FCSTD DOCUMENT  (FreeCAD 0.22R37100 (Git))
Label: composit_full_size3_model
License: All rights reserved
LicenseURL: http://en.wikipedia.org/wiki/All_rights_reserved
objects: App::Link×22, App::DocumentObjectGroup×4, Part::FeaturePython×4, App::AnnotationLabel×3, PartDesign::CoordinateSystem×1, App::FeaturePython×1, App::Part×1
note: 5 computed .brp shape members not serialized (recipe doc carries the construction recipe); baked Part::Feature solids carry a one-line shape summary decoded from their .brp
EXTERNAL_REF file=composit_full_size3.FCStd obj=Local_CS006
EXTERNAL_REF file=composit_full_size3.FCStd obj=Local_CS024
EXTERNAL_REF file=composit_full_size3.FCStd obj=Body141
EXTERNAL_REF file=composit_full_size3.FCStd obj=Local_CS008
EXTERNAL_REF file=composit_full_size3.FCStd obj=Local_CS009
EXTERNAL_REF file=composit_full_size3.FCStd obj=Body145
EXTERNAL_REF file=composit_full_size3.FCStd obj=Local_CS005
EXTERNAL_REF file=composit_full_size3.FCStd obj=Local_CS007
EXTERNAL_REF file=composit_full_size3.FCStd obj=Body144
EXTERNAL_REF file=composit_full_size3.FCStd obj=Local_CS018
EXTERNAL_REF file=composit_full_size3.FCStd obj=Body008
EXTERNAL_REF file=composit_full_size3.FCStd obj=Local_CS017
EXTERNAL_REF file=composit_full_size3.FCStd obj=Local_CS020
EXTERNAL_REF file=composit_full_size3.FCStd obj=Body006
EXTERNAL_REF file=composit_full_size3.FCStd obj=Local_CS019
EXTERNAL_REF file=composit_full_size3.FCStd obj=Local_CS022
EXTERNAL_REF file=composit_full_size3.FCStd obj=Body105
EXTERNAL_REF file=composit_full_size3.FCStd obj=Local_CS021
EXTERNAL_REF file=hub2108.FCStd obj=Local_CS001
EXTERNAL_REF file=hub2108.FCStd obj=Body
EXTERNAL_REF file=composit_full_size3.FCStd obj=Local_CS013
EXTERNAL_REF file=hub2108.FCStd obj=Local_CS
EXTERNAL_REF file=composit_full_size3.FCStd obj=Body009
EXTERNAL_REF file=composit_full_size3.FCStd obj=Local_CS011
EXTERNAL_REF file=composit_full_size3.FCStd obj=Local_CS012
EXTERNAL_REF file=composit_full_size3.FCStd obj=Body007
EXTERNAL_REF file=composit_full_size3.FCStd obj=Local_CS010
EXTERNAL_REF file=composit_full_size3.FCStd obj=Local_CS015
EXTERNAL_REF file=composit_full_size3.FCStd obj=Body107
EXTERNAL_REF file=composit_full_size3.FCStd obj=Local_CS025
EXTERNAL_REF file=composit_full_size3.FCStd obj=Body
EXTERNAL_REF file=composit_full_size3.FCStd obj=Local_CS027
EXTERNAL_REF file=composit_full_size3.FCStd obj=Body001
EXTERNAL_REF file=composit_full_size3.FCStd obj=Local_CS026
EXTERNAL_REF file=composit_full_size3.FCStd obj=Local_CS029
EXTERNAL_REF file=composit_full_size3.FCStd obj=Body004
EXTERNAL_REF file=composit_full_size3.FCStd obj=Local_CS030
EXTERNAL_REF file=composit_full_size3.FCStd obj=Local_CS032
EXTERNAL_REF file=composit_full_size3.FCStd obj=Body110
EXTERNAL_REF file=composit_full_size3.FCStd obj=Local_CS038
EXTERNAL_REF file=composit_full_size3.FCStd obj=Local_CS040
EXTERNAL_REF file=composit_full_size3.FCStd obj=Body142
EXTERNAL_REF file=composit_full_size3.FCStd obj=Local_CS031
EXTERNAL_REF file=composit_full_size3.FCStd obj=Local_CS039
EXTERNAL_REF file=composit_full_size3.FCStd obj=Body123
EXTERNAL_REF file=composit_full_size3.FCStd obj=Local_CS023
EXTERNAL_REF file=composit_full_size3.FCStd obj=Local_CS043
EXTERNAL_REF file=composit_full_size3.FCStd obj=Body147
EXTERNAL_REF file=composit_full_size3.FCStd obj=Local_CS044
EXTERNAL_REF file=composit_full_size3.FCStd obj=Body143
EXTERNAL_REF file=composit_full_size3.FCStd obj=Local_CS047
EXTERNAL_REF file=composit_full_size3.FCStd obj=pillar_bottom_LCS
EXTERNAL_REF file=composit_full_size3.FCStd obj=Body011
EXTERNAL_REF file=composit_full_size3.FCStd obj=Local_CS049
EXTERNAL_REF file=composit_full_size3.FCStd obj=Body152
EXTERNAL_REF file=composit_full_size3.FCStd obj=Local_CS050
EXTERNAL_REF file=composit_full_size3.FCStd obj=Body146

FEATURE [App::DocumentObjectGroup] Parts
FEATURE [PartDesign::CoordinateSystem] LCS_Origin
  AttacherType = Attacher::AttachEngine3D
  AttachmentSupport = -> [X_Axis]
  MapMode = 2
FEATURE [App::DocumentObjectGroup] Constraints
FEATURE [App::FeaturePython] Variables  # WARN: FeaturePython — macro-defined, semantics opaque (R4)
  Type = App::PropertyContainer
FEATURE [App::DocumentObjectGroup] Configurations
FEATURE [App::Link] pillar3
  AttachedBy = #Local_CS006
  AttachedTo = basement_bottom_proxy#Local_CS024
  LinkPlacement = pos=(332.554,-192,-90) rot=(0,0,1;1.0472rad)
  LinkedObject = -> <external composit_full_size3.FCStd>#Body141
  Placement = pos=(332.554,-192,-90) rot=(0,0,1;1.0472rad)
  SolverId = Asm4EE
  expr: Placement = basement_bottom_proxy.Placement * composit_full_size3#Local_CS024.Placement * AttachmentOffset * composit_full_size3#Local_CS006.Placement ^ -1
FEATURE [App::Link] pilllar3_dec_corner
  AttachedBy = #Local_CS008
  AttachedTo = pillar3#Local_CS009
  LinkPlacement = pos=(332.554,-192,380) rot=(0,0,1;1.0472rad)
  LinkedObject = -> <external composit_full_size3.FCStd>#Body145
  Placement = pos=(332.554,-192,380) rot=(0,0,1;1.0472rad)
  SolverId = Asm4EE
  expr: Placement = pillar3.Placement * composit_full_size3#Local_CS009.Placement * AttachmentOffset * composit_full_size3#Local_CS008.Placement ^ -1
FEATURE [App::Link] pillar3_hat_fix
  AttachedBy = #Local_CS005
  AttachedTo = pillar3#Local_CS007
  LinkPlacement = pos=(330.822,-191,1504) rot=(0,0,1;1.0472rad)
  LinkedObject = -> <external composit_full_size3.FCStd>#Body144
  Placement = pos=(330.822,-191,1504) rot=(0,0,1;1.0472rad)
  SolverId = Asm4EE
  expr: Placement = pillar3.Placement * composit_full_size3#Local_CS007.Placement * AttachmentOffset * composit_full_size3#Local_CS005.Placement ^ -1
FEATURE [App::Link] basement_top_proxy
  AttachedBy = #Local_CS018
  AttachedTo = Parent Assembly#LCS_Origin
  LinkPlacement = pos=(0,0,-3) rot=(0,0,1;0rad)
  LinkedObject = -> <external composit_full_size3.FCStd>#Body008
  Placement = pos=(0,0,-3) rot=(0,0,1;0rad)
  SolverId = Asm4EE
  expr: Placement = LCS_Origin.Placement * AttachmentOffset * composit_full_size3#Local_CS018.Placement ^ -1
FEATURE [App::Link] basement_top_plywood
  AttachedBy = #Local_CS020
  AttachedTo = basement_top_proxy#Local_CS017
  LinkPlacement = pos=(0,0,-21) rot=(0,0,1;0rad)
  LinkedObject = -> <external composit_full_size3.FCStd>#Body006
  Placement = pos=(0,0,-21) rot=(0,0,1;0rad)
  SolverId = Asm4EE
  expr: Placement = basement_top_proxy.Placement * composit_full_size3#Local_CS017.Placement * AttachmentOffset * composit_full_size3#Local_CS020.Placement ^ -1
FEATURE [App::Link] basement_top_amplifier_material_0_50ansi  label="basement_top_amplifier_material_0.50ansi"
  AttachedBy = #Local_CS022
  AttachedTo = basement_top_plywood#Local_CS019
  LinkPlacement = pos=(0,0,-23) rot=(0,0,1;0rad)
  LinkedObject = -> <external composit_full_size3.FCStd>#Body105
  Placement = pos=(0,0,-23) rot=(0,0,1;0rad)
  SolverId = Asm4EE
  expr: Placement = basement_top_plywood.Placement * composit_full_size3#Local_CS019.Placement * AttachmentOffset * composit_full_size3#Local_CS022.Placement ^ -1
FEATURE [App::Link] hub2108
  AttachedBy = #Local_CS001
  AttachedTo = basement_top_amplifier_material_0_50ansi#Local_CS021
  LinkPlacement = pos=(0,0,-90) rot=(0,0,1;0rad)
  LinkedObject = -> <external hub2108.FCStd>#Body
  Placement = pos=(0,0,-90) rot=(0,0,1;0rad)
  SolverId = Asm4EE
  expr: Placement = basement_top_amplifier_material_0_50ansi.Placement * composit_full_size3#Local_CS021.Placement * AttachmentOffset * hub2108#Local_CS001.Placement ^ -1
FEATURE [App::Link] basement_bottom_proxy
  AttachedBy = #Local_CS013
  AttachedTo = hub2108#Local_CS
  LinkPlacement = pos=(0,0,-93) rot=(0,0,1;0rad)
  LinkedObject = -> <external composit_full_size3.FCStd>#Body009
  Placement = pos=(0,0,-93) rot=(0,0,1;0rad)
  SolverId = Asm4EE
  expr: Placement = hub2108.Placement * hub2108#Local_CS.Placement * AttachmentOffset * composit_full_size3#Local_CS013.Placement ^ -1
FEATURE [App::Link] basement_bottom_plywood
  AttachedBy = #Local_CS011
  AttachedTo = basement_bottom_proxy#Local_CS012
  LinkPlacement = pos=(0,0,-111) rot=(0,0,1;0rad)
  LinkedObject = -> <external composit_full_size3.FCStd>#Body007
  Placement = pos=(0,0,-111) rot=(0,0,1;0rad)
  SolverId = Asm4EE
  expr: Placement = basement_bottom_proxy.Placement * composit_full_size3#Local_CS012.Placement * AttachmentOffset * composit_full_size3#Local_CS011.Placement ^ -1
FEATURE [App::Link] basement_bottom_amplifier_material_0_50ansi  label="basement_bottom_amplifier_material_0.50ansi"
  AttachedBy = #Local_CS015
  AttachedTo = basement_bottom_plywood#Local_CS010
  LinkPlacement = pos=(0,0,-113) rot=(0,0,1;0rad)
  LinkedObject = -> <external composit_full_size3.FCStd>#Body107
  Placement = pos=(0,0,-113) rot=(0,0,1;0rad)
  SolverId = Asm4EE
  expr: Placement = basement_bottom_plywood.Placement * composit_full_size3#Local_CS010.Placement * AttachmentOffset * composit_full_size3#Local_CS015.Placement ^ -1
FEATURE [App::Link] part1_material_0_30ansi  label="part1_material_0.30ansi"
  AttachedBy = #Local_CS025
  AttachedTo = basement_top_proxy#Local_CS018
  AttachmentOffset = pos=(0,0,0) rot=(0,0,1;4.18879rad)
  LinkPlacement = pos=(0,0,0) rot=(0,0,1;4.18879rad)
  LinkedObject = -> <external composit_full_size3.FCStd>#Body
  Placement = pos=(0,0,0) rot=(0,0,1;4.18879rad)
  SolverId = Asm4EE
  expr: Placement = basement_top_proxy.Placement * composit_full_size3#Local_CS018.Placement * AttachmentOffset * composit_full_size3#Local_CS025.Placement ^ -1
FEATURE [App::Link] part2_material_0_30ansi  label="part2_material_0.30ansi"
  AttachedBy = #Local_CS027
  AttachedTo = part1_material_0_30ansi#Local_CS025
  AttachmentOffset = pos=(0,0,0) rot=(0,0,1;2.0944rad)
  LinkPlacement = pos=(0,0,0) rot=(0,0,1;4.18879rad)
  LinkedObject = -> <external composit_full_size3.FCStd>#Body001
  Placement = pos=(0,0,0) rot=(0,0,1;4.18879rad)
  SolverId = Asm4EE
  expr: Placement = part1_material_0_30ansi.Placement * composit_full_size3#Local_CS025.Placement * AttachmentOffset * composit_full_size3#Local_CS027.Placement ^ -1
FEATURE [App::Link] dropper_fix_bottom
  AttachedBy = #Local_CS029
  AttachedTo = part1_material_0_30ansi#Local_CS026
  LinkPlacement = pos=(0,0,1428) rot=(0,0,1;4.18879rad)
  LinkedObject = -> <external composit_full_size3.FCStd>#Body004
  Placement = pos=(0,0,1428) rot=(0,0,1;4.18879rad)
  SolverId = Asm4EE
  expr: Placement = part1_material_0_30ansi.Placement * composit_full_size3#Local_CS026.Placement * AttachmentOffset * composit_full_size3#Local_CS029.Placement ^ -1
FEATURE [App::Link] dropper_fix_top
  AttachedBy = #Local_CS032
  AttachedTo = dropper_fix_bottom#Local_CS030
  AttachmentOffset = pos=(0,0,0) rot=(0,1,0;3.14159rad)
  LinkPlacement = pos=(2e-16,3e-16,1434) rot=(-0.866025,-0.5,0;3.14159rad)
  LinkedObject = -> <external composit_full_size3.FCStd>#Body110
  Placement = pos=(2e-16,3e-16,1434) rot=(-0.866025,-0.5,0;3.14159rad)
  SolverId = Asm4EE
  expr: Placement = dropper_fix_bottom.Placement * composit_full_size3#Local_CS030.Placement * AttachmentOffset * composit_full_size3#Local_CS032.Placement ^ -1
FEATURE [App::Link] hat3_bottom
  AttachedBy = #Local_CS038
  AttachedTo = sleeve_outer#Local_CS040
  AttachmentOffset = pos=(0,0,3) rot=(0,0,1;0rad)
  LinkPlacement = pos=(-1.14e-14,7e-15,1501) rot=(0,0,1;4.18879rad)
  LinkedObject = -> <external composit_full_size3.FCStd>#Body142
  Placement = pos=(-1.14e-14,7e-15,1501) rot=(0,0,1;4.18879rad)
  SolverId = Asm4EE
  expr: Placement = sleeve_outer.Placement * composit_full_size3#Local_CS040.Placement * AttachmentOffset * composit_full_size3#Local_CS038.Placement ^ -1
FEATURE [App::Link] sleeve_outer
  AttachedBy = #Local_CS039
  AttachedTo = dropper_fix_top#Local_CS031
  AttachmentOffset = pos=(0,0,0) rot=(0,-1,0;3.14159rad)
  LinkPlacement = pos=(2e-16,3e-16,1434) rot=(0,0,1;4.18879rad)
  LinkedObject = -> <external composit_full_size3.FCStd>#Body123
  Placement = pos=(2e-16,3e-16,1434) rot=(0,0,1;4.18879rad)
  SolverId = Asm4EE
  expr: Placement = dropper_fix_top.Placement * composit_full_size3#Local_CS031.Placement * AttachmentOffset * composit_full_size3#Local_CS039.Placement ^ -1
FEATURE [App::Link] pillar004
  AttachedBy = #Local_CS006
  AttachedTo = basement_bottom_proxy#Local_CS023
  LinkPlacement = pos=(-332.554,-192,-90) rot=(0,0,-1;1.0472rad)
  LinkedObject = -> <external composit_full_size3.FCStd>#Body141
  Placement = pos=(-332.554,-192,-90) rot=(0,0,-1;1.0472rad)
  SolverId = Asm4EE
  expr: Placement = basement_bottom_proxy.Placement * composit_full_size3#Local_CS023.Placement * AttachmentOffset * composit_full_size3#Local_CS006.Placement ^ -1
FEATURE [App::Link] pilllar3_dec_corner_mirror
  AttachedBy = #Local_CS043
  AttachedTo = pillar004#Local_CS009
  LinkPlacement = pos=(-332.554,-192,380) rot=(0,0,-1;1.0472rad)
  LinkedObject = -> <external composit_full_size3.FCStd>#Body147
  Placement = pos=(-332.554,-192,380) rot=(0,0,-1;1.0472rad)
  SolverId = Asm4EE
  expr: Placement = pillar004.Placement * composit_full_size3#Local_CS009.Placement * AttachmentOffset * composit_full_size3#Local_CS043.Placement ^ -1
FEATURE [App::Link] hat3_cap
  AttachedBy = #Local_CS044
  AttachedTo = sleeve_outer#Local_CS040
  AttachmentOffset = pos=(0,0,87) rot=(0,0,1;0rad)
  LinkPlacement = pos=(-2.65e-14,1.57e-14,1588) rot=(0,0,1;4.18879rad)
  LinkedObject = -> <external composit_full_size3.FCStd>#Body143
  Placement = pos=(-2.65e-14,1.57e-14,1588) rot=(0,0,1;4.18879rad)
  SolverId = Asm4EE
  expr: Placement = sleeve_outer.Placement * composit_full_size3#Local_CS040.Placement * AttachmentOffset * composit_full_size3#Local_CS044.Placement ^ -1
FEATURE [App::Link] pillar_bottom_material_0_30ansi  label="pillar_bottom_material_0.30ansi"
  AttachedBy = #pillar_bottom_LCS
  AttachedTo = pillar3#Local_CS047
  LinkPlacement = pos=(294.505,-148.902,-90) rot=(0,0,1;2.61799rad)
  LinkedObject = -> <external composit_full_size3.FCStd>#Body011
  Placement = pos=(294.505,-148.902,-90) rot=(0,0,1;2.61799rad)
  SolverId = Asm4EE
  expr: Placement = pillar3.Placement * composit_full_size3#Local_CS047.Placement * AttachmentOffset * composit_full_size3#pillar_bottom_LCS.Placement ^ -1
FEATURE [App::Link] pillar3_plexiglass_outer
  AttachedBy = #Local_CS049
  AttachedTo = Parent Assembly#LCS_Origin
  AttachmentOffset = pos=(0,0,380) rot=(0,0,1;0rad)
  LinkPlacement = pos=(0,0,380) rot=(0,0,1;0rad)
  LinkedObject = -> <external composit_full_size3.FCStd>#Body152
  Placement = pos=(0,0,380) rot=(0,0,1;0rad)
  SolverId = Asm4EE
  expr: Placement = LCS_Origin.Placement * AttachmentOffset * composit_full_size3#Local_CS049.Placement ^ -1
FEATURE [App::Link] hat3_plexiglass
  AttachedBy = #Local_CS050
  AttachedTo = sleeve_outer#Local_CS040
  AttachmentOffset = pos=(0,0,-7) rot=(0,0,1;0rad)
  LinkPlacement = pos=(-1.02e-14,6.3e-15,1494) rot=(0,0,1;4.18879rad)
  LinkedObject = -> <external composit_full_size3.FCStd>#Body146
  Placement = pos=(-1.02e-14,6.3e-15,1494) rot=(0,0,1;4.18879rad)
  SolverId = Asm4EE
  expr: Placement = sleeve_outer.Placement * composit_full_size3#Local_CS040.Placement * AttachmentOffset * composit_full_size3#Local_CS050.Placement ^ -1
FEATURE [App::Part] Assembly
  AssemblyType = Part::Link
  Group = -> [LCS_Origin,Constraints,Variables,Configurations,pillar3,pilllar3_dec_corner,pillar3_hat_fix,basement_top_proxy,basement_top_plywood,basement_top_amplifier_material_0_50ansi,hub2108,basement_bottom_proxy,basement_bottom_plywood,basement_bottom_amplifier_material_0_50ansi,part1_material_0_30ansi,part2_material_0_30ansi,dropper_fix_bottom,dropper_fix_top,hat3_bottom,sleeve_outer,pillar004,+5 more]
  Origin = -> Origin
  Type = Assembly
FEATURE [Part::FeaturePython] DistPoints  # WARN: FeaturePython — macro-defined, semantics opaque (R4)
FEATURE [App::AnnotationLabel] MeasureLbl
  BasePosition = (-263.483,-117.134,-55.5)
  LabelText = D = 111.0000 mm
  TextPosition = (0,0,0)
FEATURE [Part::FeaturePython] aCircle  # WARN: FeaturePython — macro-defined, semantics opaque (R4)
FEATURE [Part::FeaturePython] Radius  # WARN: FeaturePython — macro-defined, semantics opaque (R4)
FEATURE [App::AnnotationLabel] MeasureLbl001
  BasePosition = (-268.863,-158.115,0)
  LabelText = R = 2,5000 mm
  TextPosition = (0,0,0)
FEATURE [Part::FeaturePython] DistPoints001  # WARN: FeaturePython — macro-defined, semantics opaque (R4)
FEATURE [App::AnnotationLabel] MeasureLbl002
  BasePosition = (-287.118,-165.768,0)
  LabelText = D = 39,2713 mm
  TextPosition = (0,0,0)
FEATURE [App::DocumentObjectGroup] Measures
  Group = -> [DistPoints,MeasureLbl,aCircle,Radius,MeasureLbl001,DistPoints001,MeasureLbl002]

RESOLVED EXTERNAL PARTS (link-assembly join: the EXTERNAL_REF files above that resolve inside this repo's crawl, each included once):
---- part composit_full_size3.FCStd = doc fcstd_eedd87f2b88b (600288 chars; too large to inline — full recipe in that document) ----
---- part hub2108.FCStd = doc fcstd_856699a5e2c1 ----
FCSTD DOCUMENT  (FreeCAD 1.1R38827 (Git))
Label: hub2108
License: All rights reserved
LicenseURL: http://en.wikipedia.org/wiki/All_rights_reserved
objects: Sketcher::SketchObject×5, PartDesign::CoordinateSystem×2, PartDesign::AdditiveCylinder×1, PartDesign::Body×1
note: 16 computed .brp shape members not serialized (recipe doc carries the construction recipe); baked Part::Feature solids carry a one-line shape summary decoded from their .brp

FEATURE [Sketcher::SketchObject] Sketch  label="top_fix_holes"
  ArcFitTolerance = 0
  FullyConstrained = true
  MakeInternals = false
  expr: Constraints[6] = (58.8 mm + 38 mm) / 2
  expr: Constraints[7] = (87.5 mm + 66.67 mm) / 2
  expr: Constraints[8] = (76.14 mm + 96.68 mm) / 2
  sketch-geometry (5):
    g0: Circle CenterX=38.5425 CenterY=-28.0433 CenterZ=0 NormalX=0 NormalY=0 NormalZ=1 AngleXU=0 Radius=5.1
    g1: Circle CenterX=43.205 CenterY=20.1316 CenterZ=0 NormalX=0 NormalY=0 NormalZ=1 AngleXU=0 Radius=5.1
    g2: Circle CenterX=-43.205 CenterY=20.1316 CenterZ=0 NormalX=0 NormalY=0 NormalZ=1 AngleXU=0 Radius=5.1
    g3: Circle CenterX=-38.5425 CenterY=-28.0433 CenterZ=0 NormalX=0 NormalY=0 NormalZ=1 AngleXU=0 Radius=5.1
    g4: Circle [constr] CenterX=0 CenterY=0 CenterZ=0 NormalX=0 NormalY=0 NormalZ=1 AngleXU=0 Radius=47.665
  constraints (13):
    c: Equal(g3,g2)
    c: Equal(g3,g1)
    c: Equal(g3,g0)
    c: Diameter(g3) = 10.2
    c: Symmetric(g0,g3,g-2)
    c: Symmetric(g1,g2,g-2)
    c: Distance(g0,g1) = 48.4
    c: Distance(g0,g3) = 77.085
    c: Distance(g2,g1) = 86.41
    c: Coincident(g4,g-1)
    c: PointOnObject(g0,g4)
    c: Distance(g3,g1) = 94.8866
    c: PointOnObject(g1,g4)
FEATURE [Sketcher::SketchObject] Sketch001  label="top_center_hole"
  ArcFitTolerance = 0
  FullyConstrained = true
  MakeInternals = false
  sketch-geometry (1):
    g0: Circle CenterX=0 CenterY=0 CenterZ=0 NormalX=0 NormalY=0 NormalZ=1 AngleXU=0 Radius=28
  constraints (2):
    c: Coincident(g0,g-1)
    c: Diameter(g0) = 56
FEATURE [Sketcher::SketchObject] Sketch002  label="bottom_fix_holes"
  ArcFitTolerance = 0
  FullyConstrained = true
  MakeInternals = false
  expr: Constraints[7] = (80 mm + 58.3 mm) / 4
  sketch-geometry (6):
    g0: Circle CenterX=34.575 CenterY=34.575 CenterZ=0 NormalX=0 NormalY=0 NormalZ=1 AngleXU=0 Radius=5.4
    g1: LineSegment [constr] StartX=34.575 StartY=34.575 StartZ=0 EndX=34.575 EndY=0 EndZ=0
    g2: LineSegment [constr] StartX=34.575 StartY=34.575 StartZ=0 EndX=0 EndY=34.575 EndZ=0
    g3: Circle CenterX=-34.575 CenterY=34.575 CenterZ=0 NormalX=0 NormalY=0 NormalZ=1 AngleXU=0 Radius=5.4
    g4: Circle CenterX=-34.575 CenterY=-34.575 CenterZ=0 NormalX=0 NormalY=0 NormalZ=1 AngleXU=0 Radius=5.4
    g5: Circle CenterX=34.575 CenterY=-34.575 CenterZ=0 NormalX=0 NormalY=0 NormalZ=1 AngleXU=0 Radius=5.4
  constraints (15):
    c: Coincident(g1,g0)
    c: PointOnObject(g1,g-1)
    c: Vertical(g1)
    c: Coincident(g2,g0)
    c: PointOnObject(g2,g-2)
    c: Horizontal(g2)
    c: Equal(g1,g2)
    c: DistanceY(g1,g1) = 34.575
    c: Diameter(g0) = 10.8
    c: Symmetric(g5,g0,g-1)
    c: Symmetric(g3,g0,g-2)
    c: Symmetric(g0,g4,g-1)
    c: Equal(g0,g5)
    c: Equal(g5,g4)
    c: Equal(g4,g3)
FEATURE [Sketcher::SketchObject] Sketch003  label="bottom_center_hole"
  ArcFitTolerance = 0
  FullyConstrained = true
  MakeInternals = false
  sketch-geometry (1):
    g0: Circle CenterX=0 CenterY=0 CenterZ=0 NormalX=0 NormalY=0 NormalZ=1 AngleXU=0 Radius=30.2
  constraints (2):
    c: Coincident(g0,g-1)
    c: Diameter(g0) = 60.4
FEATURE [PartDesign::AdditiveCylinder] Cylinder
  Angle = 360
  AttacherType = Attacher::AttachEngine3D
  AttachmentSupport = -> [XY_Plane]
  FirstAngle = 0
  Height = 67
  MapMode = 5
  Radius = 58
  SecondAngle = 0
  Suppressed = false
FEATURE [PartDesign::CoordinateSystem] Local_CS  label="bottom"
  AttacherType = Attacher::AttachEngine3D
  AttachmentSupport = -> [XY_Plane]
  MapMode = 5
FEATURE [PartDesign::CoordinateSystem] Local_CS001  label="top"
  AttacherType = Attacher::AttachEngine3D
  AttachmentOffset = pos=(0,0,67) rot=(0,0,1;0rad)
  AttachmentSupport = -> [XY_Plane]
  MapMode = 5
  Placement = pos=(0,0,67) rot=(0,0,1;0rad)
  expr: .AttachmentOffset.Base.z = Cylinder.Height
FEATURE [Sketcher::SketchObject] Sketch004
  ArcFitTolerance = 0
  AttachmentSupport = -> [XY_Plane]
  FullyConstrained = false
  MakeInternals = false
  MapMode = 5
  sketch-geometry (1):
    g0: Circle CenterX=0 CenterY=-2.41744 CenterZ=0 NormalX=0 NormalY=0 NormalZ=1 AngleXU=0 Radius=27.7935
  constraints (1):
    c: PointOnObject(g0,g-2)
FEATURE [PartDesign::Body] Body  label="hub2108"
  AllowCompound = false
  Group = -> [Cylinder,Local_CS,Local_CS001,Sketch004]
  Origin = -> Origin
  Tip = -> Cylinder
